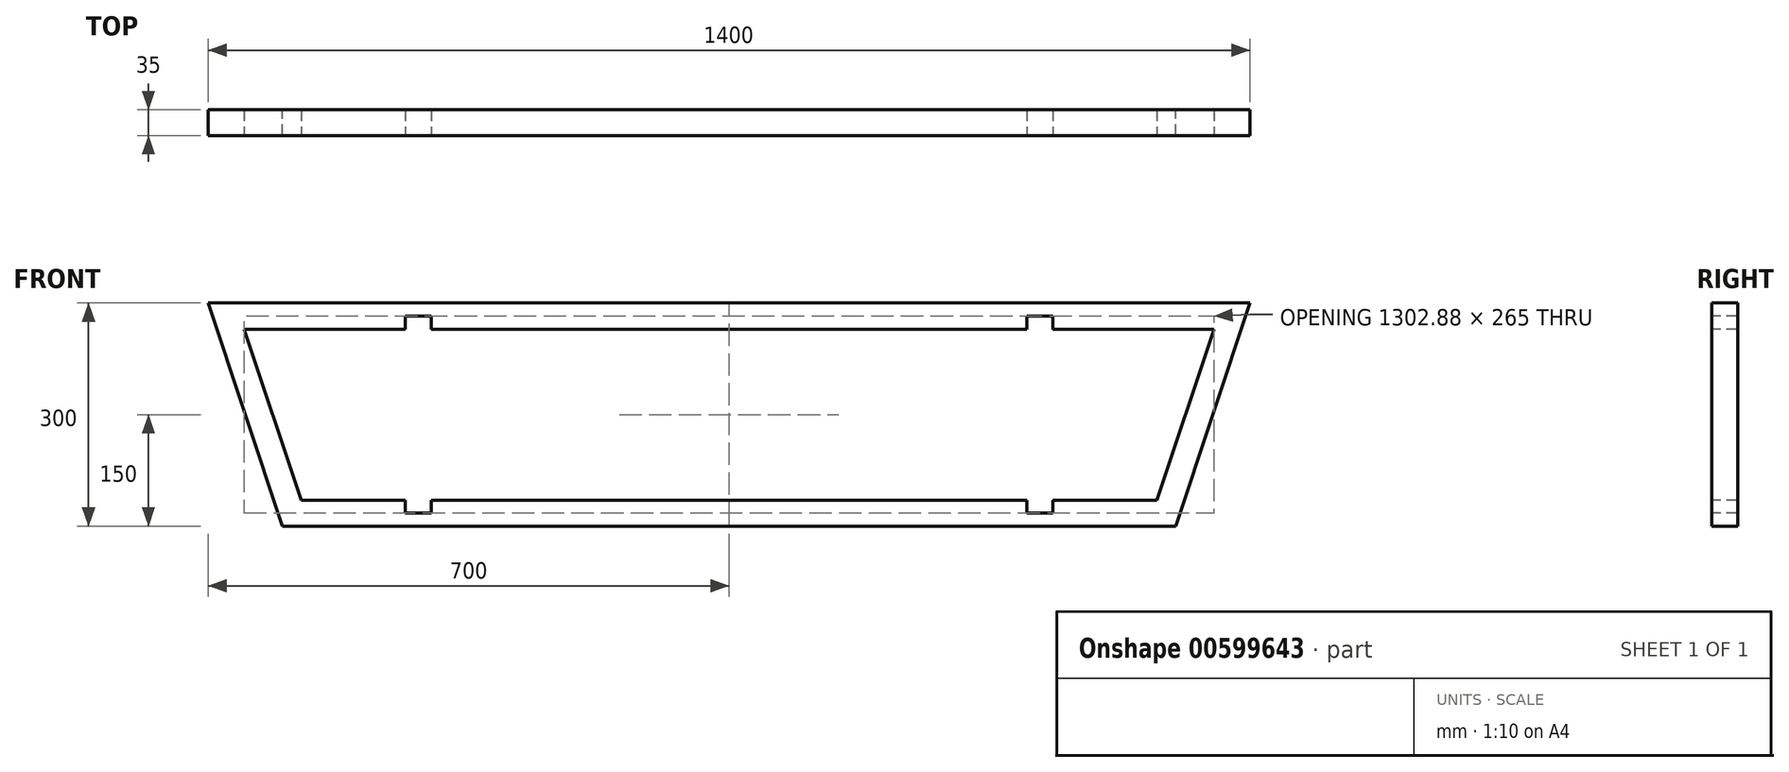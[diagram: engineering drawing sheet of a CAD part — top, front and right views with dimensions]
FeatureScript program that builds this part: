
annotation { "Feature Type Name" : "Feature", "Feature Type Description" : "" }
export const myFeature = defineFeature(function(context is Context, id is Id, definition is map)
    precondition{}
    {
        {
            var Q0;
            Q0=qCreatedBy(makeId("Front.planeOp"),FACE);
            var sketch = newSketch(context, id + "F0", { "sketchPlane" : qUnion([Q0])});
            skLineSegment(sketch, "E0", {"start": v(-700, 150) * mm, "end": v(700, 150) * mm});
            skLineSegment(sketch, "E1", {"start": v(700, 150) * mm, "end": v(600, -150) * mm});
            skLineSegment(sketch, "E2", {"start": v(600, -150) * mm, "end": v(-600, -150) * mm});
            skLineSegment(sketch, "E3", {"start": v(-600, -150) * mm, "end": v(-700, 150) * mm});
            skSolve(sketch);
        }
        {
            var Q0;
            Q0=makeQuery(id+"F0.imprint","IMPRINT",FACE,{"disambiguationData":[TD([[makeQuery(id+"F0.imprint","IMPRINT",EDGE,{"derivedFrom":sQuery(id+"F0.wireOp",EDGE,"E0")}),-1.0]])]});
            var sketch = newSketch(context, id + "F1", { "sketchPlane" : qUnion([Q0])});
            skLineSegment(sketch, "E4", {"start": v(-651.44, 115) * mm, "end": v(651.44, 115) * mm});
            skLineSegment(sketch, "E5", {"start": v(651.44, 115) * mm, "end": v(574.77, -115) * mm});
            skLineSegment(sketch, "E6", {"start": v(574.77, -115) * mm, "end": v(-574.77, -115) * mm});
            skLineSegment(sketch, "E7", {"start": v(-574.77, -115) * mm, "end": v(-651.44, 115) * mm});
            skSolve(sketch);
        }
        {
            var Q0;
            Q0 = qSketchRegion(id + "F0", true);
            extrude(context, id + "F2", {"entities" : qUnion([Q0]), "endBound" : BoundingType.SYMMETRIC, "depth" : 35 * mm, "offsetDistance" : 25 * mm});
        }
        {
            var Q0;
            Q0 = qSketchRegion(id + "F1", true);
            extrude(context, id + "F3", {"entities" : qUnion([Q0]), "operationType" : NewBodyOperationType.REMOVE, "endBound" : BoundingType.SYMMETRIC, "oppositeDirection" : true, "depth" : 35 * mm, "offsetDistance" : 25 * mm});
        }
        {
            var Q0;
            Q0=makeQuery(id+"F2.opExtrude","CAP_FACE",FACE,{"disambiguationData":[OSD([sQuery(id+"F0.wireOp",EDGE,"E0"),sQuery(id+"F0.wireOp",EDGE,"E1"),sQuery(id+"F0.wireOp",EDGE,"E2"),sQuery(id+"F0.wireOp",EDGE,"E3")])],"isStart":false});
            var sketch = newSketch(context, id + "F4", { "sketchPlane" : qUnion([Q0])});
            skLineSegment(sketch, "E8.bottom", {"start": v(-435, -115) * mm, "end": v(-400, -115) * mm});
            skLineSegment(sketch, "E8.top", {"start": v(-435, -132.5) * mm, "end": v(-400, -132.5) * mm});
            skLineSegment(sketch, "E8.left", {"start": v(-435, -115) * mm, "end": v(-435, -132.5) * mm});
            skLineSegment(sketch, "E8.right", {"start": v(-400, -115) * mm, "end": v(-400, -132.5) * mm});
            skSolve(sketch);
        }
        {
            var Q0;
            Q0 = qSketchRegion(id + "F4", true);
            extrude(context, id + "F5", {"entities" : qUnion([Q0]), "operationType" : NewBodyOperationType.REMOVE, "oppositeDirection" : true, "depth" : 35 * mm, "offsetDistance" : 25 * mm});
        }
        {
            var Q0;
            Q0=makeQuery(id+"F2.opExtrude","CAP_FACE",FACE,{"disambiguationData":[OSD([sQuery(id+"F0.wireOp",EDGE,"E0"),sQuery(id+"F0.wireOp",EDGE,"E1"),sQuery(id+"F0.wireOp",EDGE,"E2"),sQuery(id+"F0.wireOp",EDGE,"E3")])],"isStart":false});
            var sketch = newSketch(context, id + "F6", { "sketchPlane" : qUnion([Q0])});
            skLineSegment(sketch, "E9.bottom", {"start": v(400, -115) * mm, "end": v(435, -115) * mm});
            skLineSegment(sketch, "E9.top", {"start": v(400, -132.5) * mm, "end": v(435, -132.5) * mm});
            skLineSegment(sketch, "E9.left", {"start": v(400, -115) * mm, "end": v(400, -132.5) * mm});
            skLineSegment(sketch, "E9.right", {"start": v(435, -115) * mm, "end": v(435, -132.5) * mm});
            skSolve(sketch);
        }
        {
            var Q0;
            Q0 = qSketchRegion(id + "F6", true);
            extrude(context, id + "F7", {"entities" : qUnion([Q0]), "operationType" : NewBodyOperationType.REMOVE, "oppositeDirection" : true, "depth" : 35 * mm, "offsetDistance" : 25 * mm});
        }
        {
            var Q0;
            Q0=makeQuery(id+"F2.opExtrude","CAP_FACE",FACE,{"disambiguationData":[OSD([sQuery(id+"F0.wireOp",EDGE,"E0"),sQuery(id+"F0.wireOp",EDGE,"E1"),sQuery(id+"F0.wireOp",EDGE,"E2"),sQuery(id+"F0.wireOp",EDGE,"E3")])],"isStart":false});
            var sketch = newSketch(context, id + "F8", { "sketchPlane" : qUnion([Q0])});
            skLineSegment(sketch, "E10.bottom", {"start": v(-435, 115) * mm, "end": v(-400, 115) * mm});
            skLineSegment(sketch, "E10.top", {"start": v(-435, 132.5) * mm, "end": v(-400, 132.5) * mm});
            skLineSegment(sketch, "E10.left", {"start": v(-435, 115) * mm, "end": v(-435, 132.5) * mm});
            skLineSegment(sketch, "E10.right", {"start": v(-400, 115) * mm, "end": v(-400, 132.5) * mm});
            skSolve(sketch);
        }
        {
            var Q0;
            Q0 = qSketchRegion(id + "F8", true);
            extrude(context, id + "F9", {"entities" : qUnion([Q0]), "operationType" : NewBodyOperationType.REMOVE, "oppositeDirection" : true, "depth" : 35 * mm, "offsetDistance" : 25 * mm});
        }
        {
            var Q0;
            Q0=makeQuery(id+"F2.opExtrude","CAP_FACE",FACE,{"disambiguationData":[OSD([sQuery(id+"F0.wireOp",EDGE,"E0"),sQuery(id+"F0.wireOp",EDGE,"E1"),sQuery(id+"F0.wireOp",EDGE,"E2"),sQuery(id+"F0.wireOp",EDGE,"E3")])],"isStart":false});
            var sketch = newSketch(context, id + "F10", { "sketchPlane" : qUnion([Q0])});
            skLineSegment(sketch, "E11.bottom", {"start": v(400, 115) * mm, "end": v(435, 115) * mm});
            skLineSegment(sketch, "E11.top", {"start": v(400, 132.5) * mm, "end": v(435, 132.5) * mm});
            skLineSegment(sketch, "E11.left", {"start": v(400, 115) * mm, "end": v(400, 132.5) * mm});
            skLineSegment(sketch, "E11.right", {"start": v(435, 115) * mm, "end": v(435, 132.5) * mm});
            skSolve(sketch);
        }
        {
            var Q0;
            Q0 = qSketchRegion(id + "F10", true);
            extrude(context, id + "F11", {"entities" : qUnion([Q0]), "operationType" : NewBodyOperationType.REMOVE, "oppositeDirection" : true, "depth" : 35 * mm, "offsetDistance" : 25 * mm});
        }
    });
